# Revit family: Triangle Tube Ionic WCB 299
name_source: partatom
category: Mechanical Equipment
units: mm (PartAtom-declared; Revit-internal decimal feet)

## family parameters
Always vertical = Yes
Cut with Voids When Loaded = No
OmniClass Number = 23.75.00.00
OmniClass Title = Climate Control (HVAC)
Part Type = Normal
Room Calculation Point = No
Round Connector Dimension = Use Radius
Shared = No
Work Plane-Based = No

## types (1)
- Ionic WCB 299
    Air Inlet Radius = 2 "
    Air Vent Drain Radius = 0.38 "
    Back Clearance = 0 "
    Bottom Clearance = 10 "
    Buttons = Plastic Black
    Clearance A = 6 "
    Clearance D = 0 "
    Clearances = Clearance
    Clearence B = 14 "
    Clearence C = 2 "
    Clearence E = 10 "
    Condensate Drain Radius = 0.53 "
    Depth = 21.43 "
    Description = Triangle Tube Ionic WCB 299
    Display = Glass
    Flue Gas Outlet Radius = 2 "
    Front Clearance = 6 "
    Gas Connection Outlet Radius = 0.5 "
    Height = 33.27 "
    Manufacturer = Triangle Tube
    MechEq Finish = Stainless Steel - Satin
    Model = Ionic WCB 299
    Mounting Height = 25 "
    Side Clearance = 2 "
    Top Clearance = 14 "
    Water Inlet Radius = 0.75 "
    Water Outlet Radius = 0.75 "
    Width = 17.4 "

## geometry (parser evidence)
native form markers: Sweep x9
no freeform markers — native parametric forms only
